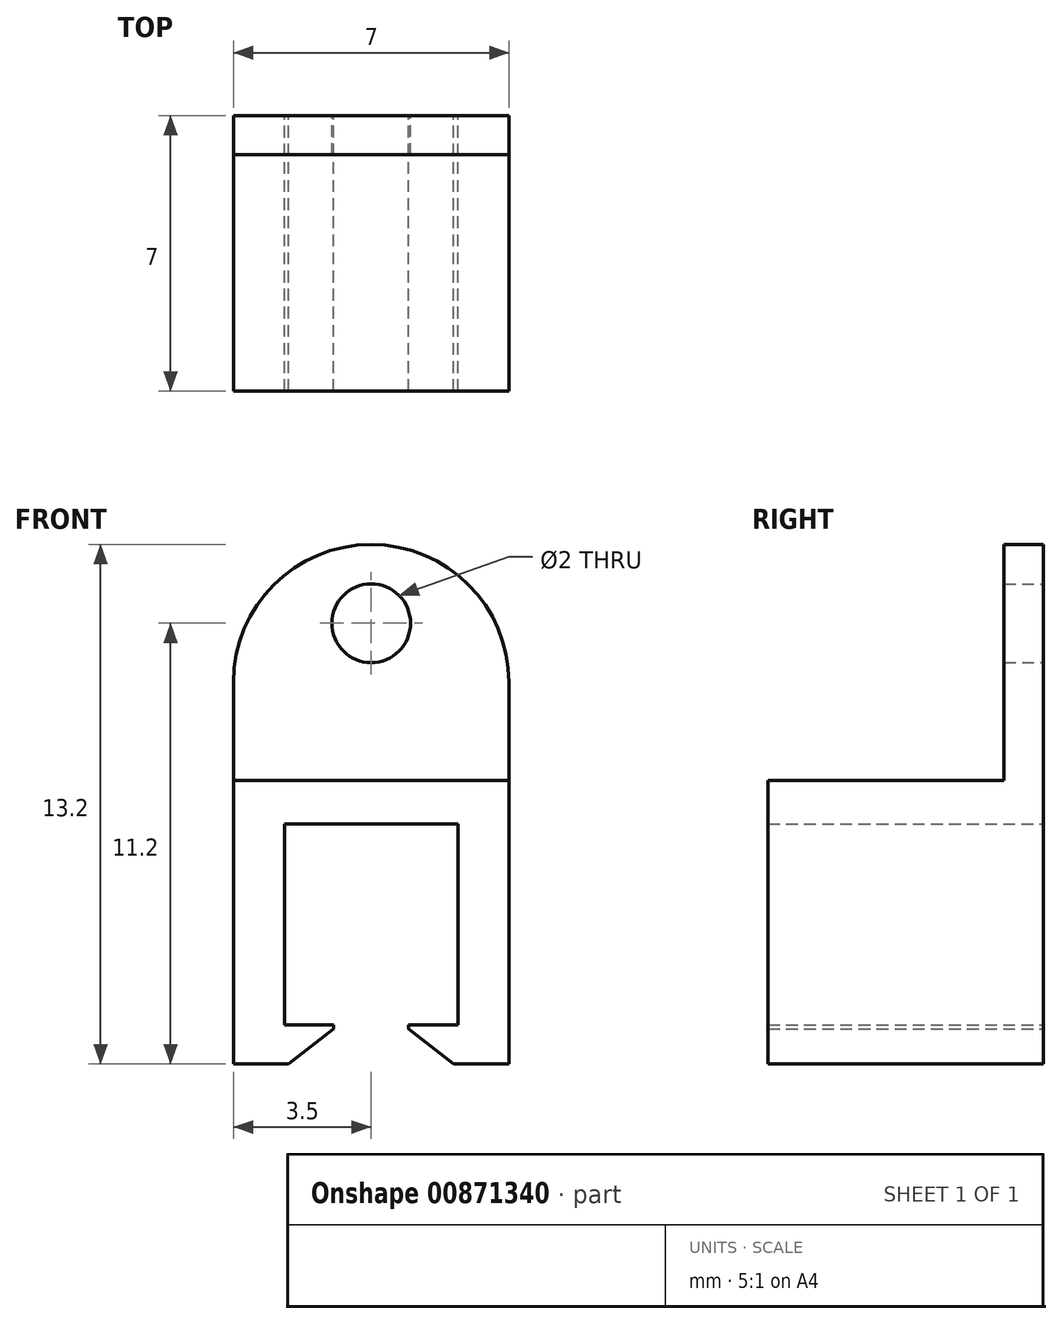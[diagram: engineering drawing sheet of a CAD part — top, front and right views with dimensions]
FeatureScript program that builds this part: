
annotation { "Feature Type Name" : "Feature", "Feature Type Description" : "" }
export const myFeature = defineFeature(function(context is Context, id is Id, definition is map)
    precondition{}
    {
        {
            var Q0;
            Q0=qCreatedBy(makeId("Front.planeOp"),FACE);
            var sketch = newSketch(context, id + "F0", { "sketchPlane" : qUnion([Q0])});
            skLineSegment(sketch, "E0", {"start": v(-2.2, -6.2) * mm, "end": v(-0.95, -6.2) * mm});
            skLineSegment(sketch, "E1", {"start": v(-0.95, -6.2) * mm, "end": v(-0.95, -6.3) * mm});
            skLineSegment(sketch, "E2", {"start": v(-2.1, -7.2) * mm, "end": v(-0.95, -6.3) * mm});
            skLineSegment(sketch, "E3", {"start": v(-2.1, -7.2) * mm, "end": v(-3.5, -7.2) * mm});
            skLineSegment(sketch, "E4", {"start": v(-3.5, -7.2) * mm, "end": v(-3.5, 0) * mm});
            skLineSegment(sketch, "E5", {"start": v(-3.5, 0) * mm, "end": v(3.5, 0) * mm});
            skLineSegment(sketch, "E6", {"start": v(3.5, 0) * mm, "end": v(3.5, -7.2) * mm});
            skLineSegment(sketch, "E7", {"start": v(3.5, -7.2) * mm, "end": v(2.1, -7.2) * mm});
            skLineSegment(sketch, "E8", {"start": v(0.95, -6.3) * mm, "end": v(2.1, -7.2) * mm});
            skLineSegment(sketch, "E9", {"start": v(0.95, -6.3) * mm, "end": v(0.95, -6.2) * mm});
            skLineSegment(sketch, "E10", {"start": v(0.95, -6.2) * mm, "end": v(2.2, -6.2) * mm});
            skLineSegment(sketch, "E11", {"start": v(2.2, -6.2) * mm, "end": v(2.2, -1.1) * mm});
            skLineSegment(sketch, "E12", {"start": v(2.2, -1.1) * mm, "end": v(-2.2, -1.1) * mm});
            skLineSegment(sketch, "E13", {"start": v(-2.2, -1.1) * mm, "end": v(-2.2, -6.2) * mm});
            skLineSegment(sketch, "E14", {"start": v(-3.5, 0) * mm, "end": v(-3.5, 2.5) * mm});
            skLineSegment(sketch, "E15", {"start": v(3.5, 0) * mm, "end": v(3.5, 2.5) * mm});
            skArc(sketch, "E16", {"start": v(3.5, 2.5) * mm, "mid": v(0, 6) * mm, "end": v(-3.5, 2.5) * mm});
            skCircle(sketch, "E17", {"center": v(0, 4) * mm, "radius": 1 * mm});
            skSolve(sketch);
        }
        {
            var Q0;
            Q0=makeQuery(id+"F0.imprint","IMPRINT",FACE,{"disambiguationData":[TD([[makeQuery(id+"F0.imprint","IMPRINT",EDGE,{"derivedFrom":sQuery(id+"F0.wireOp",EDGE,"E0")}),-1.0]])]});
            extrude(context, id + "F1", {"entities" : qUnion([Q0]), "depth" : 7 * mm, "offsetDistance" : 25 * mm});
        }
        {
            var Q0;
            Q0=makeQuery(id+"F0.imprint","IMPRINT",FACE,{"disambiguationData":[TD([[makeQuery(id+"F0.imprint","IMPRINT",EDGE,{"derivedFrom":sQuery(id+"F0.wireOp",EDGE,"E5")}),1.0]])]});
            extrude(context, id + "F2", {"entities" : qUnion([Q0]), "operationType" : NewBodyOperationType.ADD, "depth" : 1 * mm, "offsetDistance" : 25 * mm});
        }
    });
